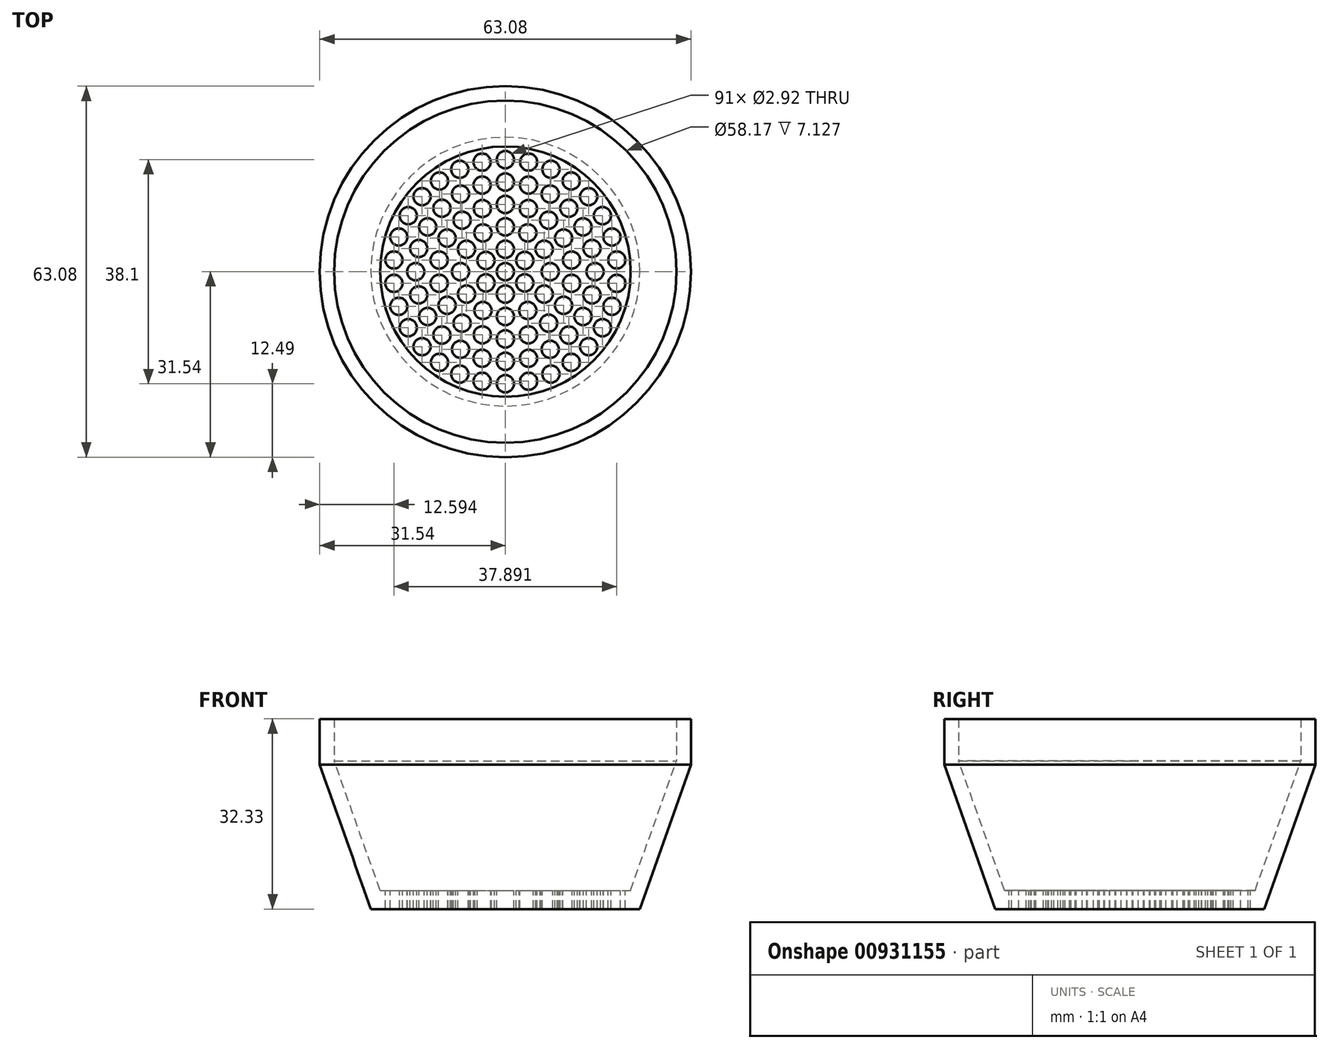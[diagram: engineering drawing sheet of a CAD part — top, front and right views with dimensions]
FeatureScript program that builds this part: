
annotation { "Feature Type Name" : "Feature", "Feature Type Description" : "" }
export const myFeature = defineFeature(function(context is Context, id is Id, definition is map)
    precondition{}
    {
        {
            var Q0;
            Q0=qCreatedBy(makeId("Top.planeOp"),FACE);
            var sketch = newSketch(context, id + "F0", { "sketchPlane" : qUnion([Q0])});
            skCircle(sketch, "E0", {"center": v(0, 0) * mm, "radius": 1.46 * mm});
            skCircle(sketch, "E1", {"center": v(0, 3.81) * mm, "radius": 1.46 * mm});
            skCircle(sketch, "E2", {"center": v(0, 7.62) * mm, "radius": 1.46 * mm});
            skCircle(sketch, "E3", {"center": v(0, 11.43) * mm, "radius": 1.46 * mm});
            skCircle(sketch, "E4", {"center": v(0, 15.24) * mm, "radius": 1.46 * mm});
            skCircle(sketch, "E5", {"center": v(0, 19.05) * mm, "radius": 1.46 * mm});
            skCircle(sketch, "E6", {"center": v(0, 0) * mm, "radius": 3.81 * mm, "construction": true});
            skCircle(sketch, "E7", {"center": v(0, 0) * mm, "radius": 7.62 * mm, "construction": true});
            skCircle(sketch, "E8", {"center": v(0, 0) * mm, "radius": 11.43 * mm, "construction": true});
            skCircle(sketch, "E9", {"center": v(0, 0) * mm, "radius": 15.24 * mm, "construction": true});
            skCircle(sketch, "E10", {"center": v(0, 0) * mm, "radius": 19.05 * mm, "construction": true});
            skCircle(sketch, "E11.1.0", {"center": v(-3.3, 1.9) * mm, "radius": 1.46 * mm});
            skCircle(sketch, "E11.2.0", {"center": v(-3.3, -1.9) * mm, "radius": 1.46 * mm});
            skCircle(sketch, "E11.3.0", {"center": v(0, -3.81) * mm, "radius": 1.46 * mm});
            skCircle(sketch, "E11.4.0", {"center": v(3.3, -1.9) * mm, "radius": 1.46 * mm});
            skCircle(sketch, "E11.5.0", {"center": v(3.3, 1.9) * mm, "radius": 1.46 * mm});
            skCircle(sketch, "E12.1.0", {"center": v(-3.8, 6.6) * mm, "radius": 1.46 * mm});
            skCircle(sketch, "E12.2.0", {"center": v(-6.6, 3.81) * mm, "radius": 1.46 * mm});
            skCircle(sketch, "E12.3.0", {"center": v(-7.62, 0) * mm, "radius": 1.46 * mm});
            skCircle(sketch, "E12.4.0", {"center": v(-6.6, -3.8) * mm, "radius": 1.46 * mm});
            skCircle(sketch, "E12.5.0", {"center": v(-3.8, -6.6) * mm, "radius": 1.46 * mm});
            skCircle(sketch, "E12.6.0", {"center": v(0, -7.62) * mm, "radius": 1.46 * mm});
            skCircle(sketch, "E12.7.0", {"center": v(3.8, -6.6) * mm, "radius": 1.46 * mm});
            skCircle(sketch, "E12.8.0", {"center": v(6.6, -3.81) * mm, "radius": 1.46 * mm});
            skCircle(sketch, "E12.9.0", {"center": v(7.62, 0) * mm, "radius": 1.46 * mm});
            skCircle(sketch, "E12.10.0", {"center": v(6.6, 3.81) * mm, "radius": 1.46 * mm});
            skCircle(sketch, "E12.11.0", {"center": v(3.81, 6.6) * mm, "radius": 1.46 * mm});
            skCircle(sketch, "E13.1.0", {"center": v(-3.9, 10.74) * mm, "radius": 1.46 * mm});
            skCircle(sketch, "E13.2.0", {"center": v(-7.35, 8.76) * mm, "radius": 1.46 * mm});
            skCircle(sketch, "E13.3.0", {"center": v(-9.9, 5.72) * mm, "radius": 1.46 * mm});
            skCircle(sketch, "E13.4.0", {"center": v(-11.26, 1.98) * mm, "radius": 1.46 * mm});
            skCircle(sketch, "E13.5.0", {"center": v(-11.26, -1.98) * mm, "radius": 1.46 * mm});
            skCircle(sketch, "E13.6.0", {"center": v(-9.9, -5.71) * mm, "radius": 1.46 * mm});
            skCircle(sketch, "E13.7.0", {"center": v(-7.35, -8.76) * mm, "radius": 1.46 * mm});
            skCircle(sketch, "E13.8.0", {"center": v(-3.9, -10.74) * mm, "radius": 1.46 * mm});
            skCircle(sketch, "E13.9.0", {"center": v(0, -11.43) * mm, "radius": 1.46 * mm});
            skCircle(sketch, "E13.10.0", {"center": v(3.9, -10.74) * mm, "radius": 1.46 * mm});
            skCircle(sketch, "E13.11.0", {"center": v(7.35, -8.76) * mm, "radius": 1.46 * mm});
            skCircle(sketch, "E13.12.0", {"center": v(9.9, -5.72) * mm, "radius": 1.46 * mm});
            skCircle(sketch, "E13.13.0", {"center": v(11.26, -1.98) * mm, "radius": 1.46 * mm});
            skCircle(sketch, "E13.14.0", {"center": v(11.26, 1.98) * mm, "radius": 1.46 * mm});
            skCircle(sketch, "E13.15.0", {"center": v(9.9, 5.71) * mm, "radius": 1.46 * mm});
            skCircle(sketch, "E13.16.0", {"center": v(7.35, 8.76) * mm, "radius": 1.46 * mm});
            skCircle(sketch, "E13.17.0", {"center": v(3.9, 10.74) * mm, "radius": 1.46 * mm});
            skCircle(sketch, "E14.1.0", {"center": v(-3.94, 14.72) * mm, "radius": 1.46 * mm});
            skCircle(sketch, "E14.2.0", {"center": v(-7.62, 13.2) * mm, "radius": 1.46 * mm});
            skCircle(sketch, "E14.3.0", {"center": v(-10.78, 10.78) * mm, "radius": 1.46 * mm});
            skCircle(sketch, "E14.4.0", {"center": v(-13.2, 7.62) * mm, "radius": 1.46 * mm});
            skCircle(sketch, "E14.5.0", {"center": v(-14.72, 3.94) * mm, "radius": 1.46 * mm});
            skCircle(sketch, "E14.6.0", {"center": v(-15.24, 0) * mm, "radius": 1.46 * mm});
            skCircle(sketch, "E14.7.0", {"center": v(-14.72, -3.94) * mm, "radius": 1.46 * mm});
            skCircle(sketch, "E14.8.0", {"center": v(-13.2, -7.62) * mm, "radius": 1.46 * mm});
            skCircle(sketch, "E14.9.0", {"center": v(-10.78, -10.78) * mm, "radius": 1.46 * mm});
            skCircle(sketch, "E14.10.0", {"center": v(-7.62, -13.2) * mm, "radius": 1.46 * mm});
            skCircle(sketch, "E14.11.0", {"center": v(-3.94, -14.72) * mm, "radius": 1.46 * mm});
            skCircle(sketch, "E14.12.0", {"center": v(0, -15.24) * mm, "radius": 1.46 * mm});
            skCircle(sketch, "E14.13.0", {"center": v(3.94, -14.72) * mm, "radius": 1.46 * mm});
            skCircle(sketch, "E14.14.0", {"center": v(7.62, -13.2) * mm, "radius": 1.46 * mm});
            skCircle(sketch, "E14.15.0", {"center": v(10.78, -10.78) * mm, "radius": 1.46 * mm});
            skCircle(sketch, "E14.16.0", {"center": v(13.2, -7.62) * mm, "radius": 1.46 * mm});
            skCircle(sketch, "E14.17.0", {"center": v(14.72, -3.94) * mm, "radius": 1.46 * mm});
            skCircle(sketch, "E14.18.0", {"center": v(15.24, 0) * mm, "radius": 1.46 * mm});
            skCircle(sketch, "E14.19.0", {"center": v(14.72, 3.94) * mm, "radius": 1.46 * mm});
            skCircle(sketch, "E14.20.0", {"center": v(13.2, 7.62) * mm, "radius": 1.46 * mm});
            skCircle(sketch, "E14.21.0", {"center": v(10.78, 10.78) * mm, "radius": 1.46 * mm});
            skCircle(sketch, "E14.22.0", {"center": v(7.62, 13.2) * mm, "radius": 1.46 * mm});
            skCircle(sketch, "E14.23.0", {"center": v(3.94, 14.72) * mm, "radius": 1.46 * mm});
            skCircle(sketch, "E15.1.0", {"center": v(-3.96, 18.63) * mm, "radius": 1.46 * mm});
            skCircle(sketch, "E15.2.0", {"center": v(-7.75, 17.4) * mm, "radius": 1.46 * mm});
            skCircle(sketch, "E15.3.0", {"center": v(-11.2, 15.41) * mm, "radius": 1.46 * mm});
            skCircle(sketch, "E15.4.0", {"center": v(-14.16, 12.75) * mm, "radius": 1.46 * mm});
            skCircle(sketch, "E15.5.0", {"center": v(-16.5, 9.53) * mm, "radius": 1.46 * mm});
            skCircle(sketch, "E15.6.0", {"center": v(-18.12, 5.89) * mm, "radius": 1.46 * mm});
            skCircle(sketch, "E15.7.0", {"center": v(-18.95, 2) * mm, "radius": 1.46 * mm});
            skCircle(sketch, "E15.8.0", {"center": v(-18.95, -2) * mm, "radius": 1.46 * mm});
            skCircle(sketch, "E15.9.0", {"center": v(-18.12, -5.89) * mm, "radius": 1.46 * mm});
            skCircle(sketch, "E15.10.0", {"center": v(-16.5, -9.52) * mm, "radius": 1.46 * mm});
            skCircle(sketch, "E15.11.0", {"center": v(-14.16, -12.75) * mm, "radius": 1.46 * mm});
            skCircle(sketch, "E15.12.0", {"center": v(-11.2, -15.41) * mm, "radius": 1.46 * mm});
            skCircle(sketch, "E15.13.0", {"center": v(-7.75, -17.4) * mm, "radius": 1.46 * mm});
            skCircle(sketch, "E15.14.0", {"center": v(-3.96, -18.63) * mm, "radius": 1.46 * mm});
            skCircle(sketch, "E15.15.0", {"center": v(0, -19.05) * mm, "radius": 1.46 * mm});
            skCircle(sketch, "E15.16.0", {"center": v(3.96, -18.63) * mm, "radius": 1.46 * mm});
            skCircle(sketch, "E15.17.0", {"center": v(7.75, -17.4) * mm, "radius": 1.46 * mm});
            skCircle(sketch, "E15.18.0", {"center": v(11.2, -15.41) * mm, "radius": 1.46 * mm});
            skCircle(sketch, "E15.19.0", {"center": v(14.16, -12.75) * mm, "radius": 1.46 * mm});
            skCircle(sketch, "E15.20.0", {"center": v(16.5, -9.53) * mm, "radius": 1.46 * mm});
            skCircle(sketch, "E15.21.0", {"center": v(18.12, -5.89) * mm, "radius": 1.46 * mm});
            skCircle(sketch, "E15.22.0", {"center": v(18.95, -2) * mm, "radius": 1.46 * mm});
            skCircle(sketch, "E15.23.0", {"center": v(18.95, 2) * mm, "radius": 1.46 * mm});
            skCircle(sketch, "E15.24.0", {"center": v(18.12, 5.89) * mm, "radius": 1.46 * mm});
            skCircle(sketch, "E15.25.0", {"center": v(16.5, 9.53) * mm, "radius": 1.46 * mm});
            skCircle(sketch, "E15.26.0", {"center": v(14.16, 12.75) * mm, "radius": 1.46 * mm});
            skCircle(sketch, "E15.27.0", {"center": v(11.2, 15.41) * mm, "radius": 1.46 * mm});
            skCircle(sketch, "E15.28.0", {"center": v(7.75, 17.4) * mm, "radius": 1.46 * mm});
            skCircle(sketch, "E15.29.0", {"center": v(3.96, 18.63) * mm, "radius": 1.46 * mm});
            skSolve(sketch);
        }
        {
            var Q0;
            Q0=qCreatedBy(makeId("Front.planeOp"),FACE);
            var sketch = newSketch(context, id + "F1", { "sketchPlane" : qUnion([Q0])});
            skLineSegment(sketch, "E16", {"start": v(0, 1.61) * mm, "end": v(21.29, 1.61) * mm});
            skLineSegment(sketch, "E17", {"start": v(21.29, 1.61) * mm, "end": v(29.08, 23.64) * mm});
            skLineSegment(sketch, "E18", {"start": v(31.54, 22.98) * mm, "end": v(22.86, -1.56) * mm});
            skLineSegment(sketch, "E19", {"start": v(22.86, -1.56) * mm, "end": v(0, -1.56) * mm});
            skLineSegment(sketch, "E20", {"start": v(0, -1.56) * mm, "end": v(0, 1.61) * mm});
            skLineSegment(sketch, "E21", {"start": v(29.08, 23.64) * mm, "end": v(29.08, 30.77) * mm});
            skLineSegment(sketch, "E22", {"start": v(29.08, 30.77) * mm, "end": v(31.54, 30.77) * mm});
            skLineSegment(sketch, "E23", {"start": v(31.54, 30.77) * mm, "end": v(31.54, 22.98) * mm});
            skSolve(sketch);
        }
        {
            var Q0;
            Q0 = qSketchRegion(id + "F1", true);
            var Q1;
            Q1=sQuery(id+"F1.wireOp",EDGE,"E20");
            revolve(context, id + "F2", {"surfaceOperationType" : NewSurfaceOperationType.NEW, "entities" : qUnion([Q0]), "axis" : qUnion([Q1]), "revolveType" : RevolveType.FULL});
        }
        {
            var Q0;
            Q0 = qSketchRegion(id + "F0", true);
            extrude(context, id + "F3", {"entities" : qUnion([Q0]), "operationType" : NewBodyOperationType.REMOVE, "endBound" : BoundingType.SYMMETRIC, "oppositeDirection" : true, "depth" : 25.4 * mm, "offsetDistance" : 25.4 * mm});
        }
    });
